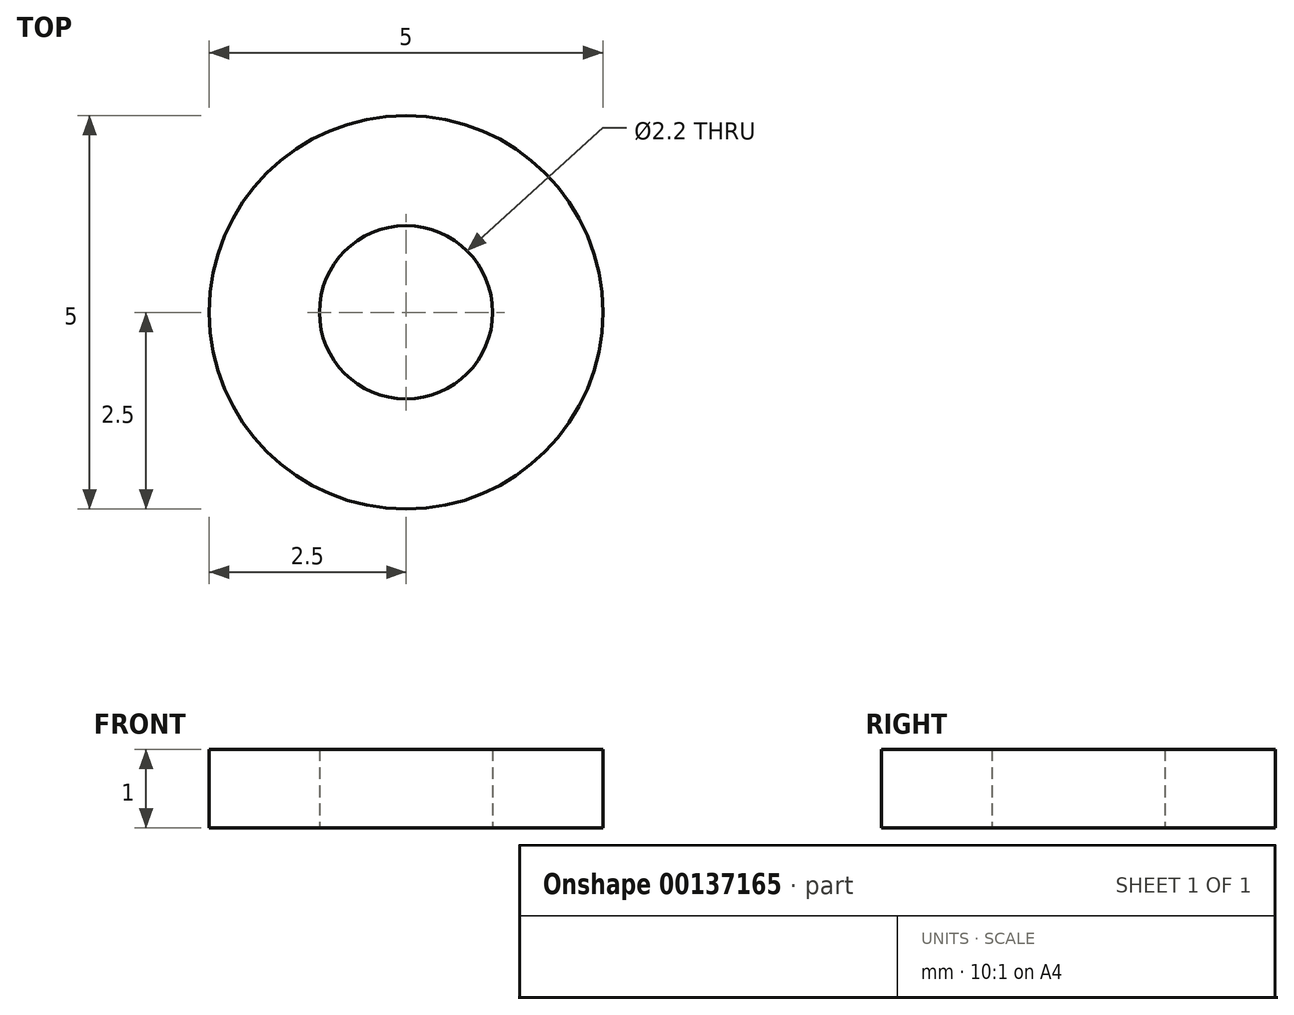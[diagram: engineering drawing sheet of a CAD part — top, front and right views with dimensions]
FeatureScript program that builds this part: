
annotation { "Feature Type Name" : "Feature", "Feature Type Description" : "" }
export const myFeature = defineFeature(function(context is Context, id is Id, definition is map)
    precondition{}
    {
        {
            var Q0;
            Q0=qCreatedBy(makeId("Top.planeOp"),FACE);
            var sketch = newSketch(context, id + "F0", { "sketchPlane" : qUnion([Q0])});
            skCircle(sketch, "E0", {"center": v(0, 0) * mm, "radius": 1.1 * mm});
            skCircle(sketch, "E1", {"center": v(0, 0) * mm, "radius": 2.5 * mm});
            skSolve(sketch);
        }
        {
            var Q0;
            Q0=qSketchRegion(id+"F0",true);
            extrude(context, id + "F1", {"entities" : qUnion([Q0]), "depth" : 1 * mm});
        }
    });
